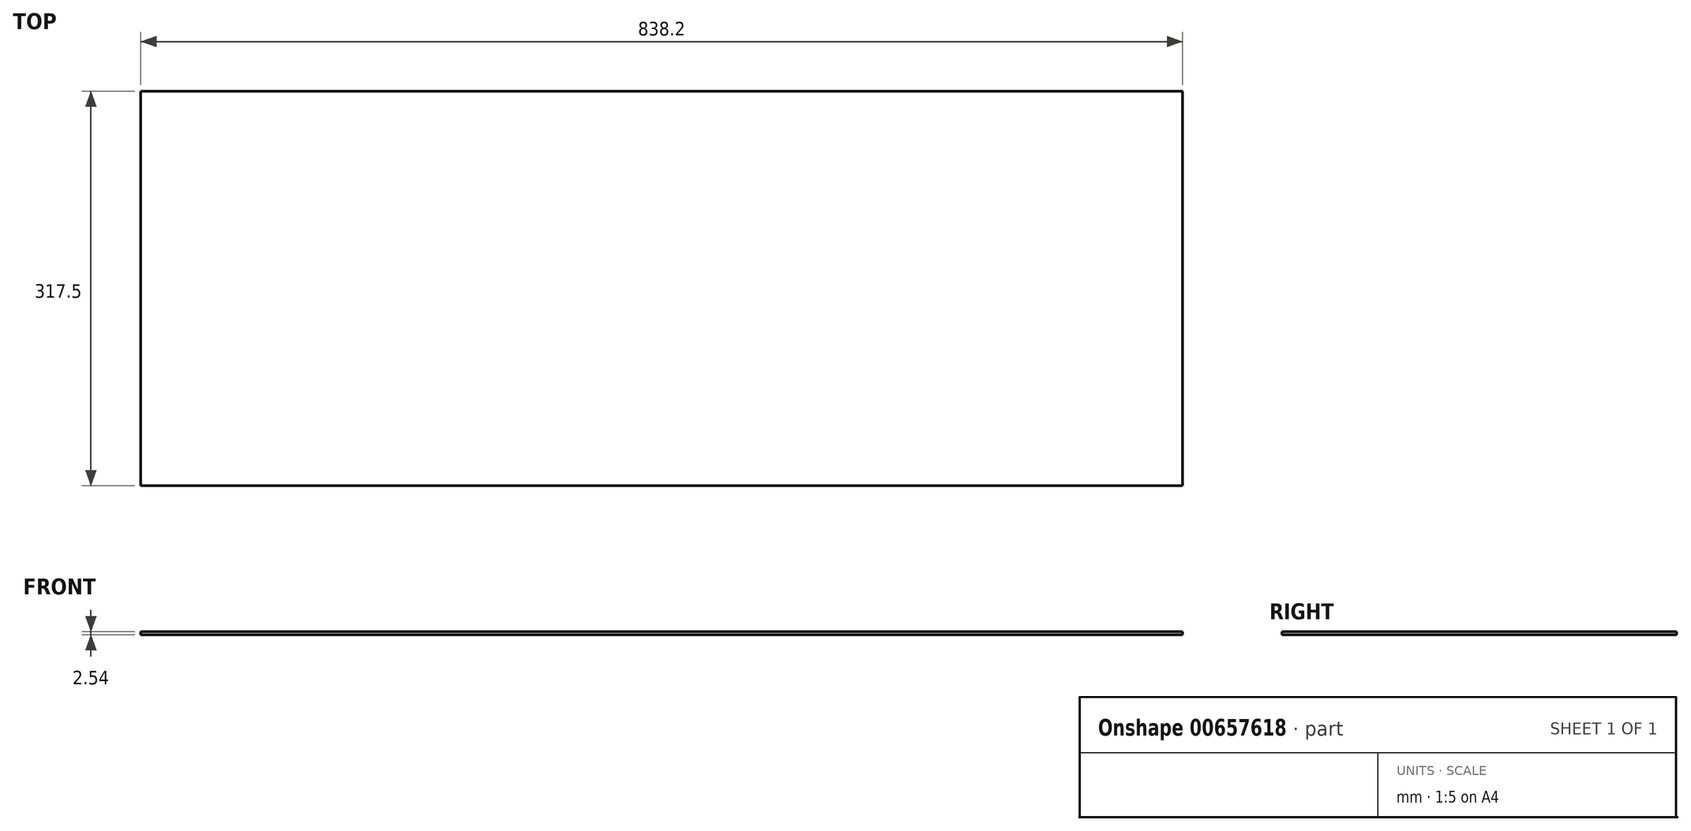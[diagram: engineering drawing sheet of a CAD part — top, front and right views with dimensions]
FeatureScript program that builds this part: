
annotation { "Feature Type Name" : "Feature", "Feature Type Description" : "" }
export const myFeature = defineFeature(function(context is Context, id is Id, definition is map)
    precondition{}
    {
        {
            var Q0;
            Q0=qCreatedBy(makeId("Top.planeOp"),FACE);
            var sketch = newSketch(context, id + "F0", { "sketchPlane" : qUnion([Q0])});
            skLineSegment(sketch, "E0.bottom", {"start": v(0, 0) * mm, "end": v(838.2, 0) * mm});
            skLineSegment(sketch, "E0.top", {"start": v(0, -317.5) * mm, "end": v(838.2, -317.5) * mm});
            skLineSegment(sketch, "E0.left", {"start": v(0, 0) * mm, "end": v(0, -317.5) * mm});
            skLineSegment(sketch, "E0.right", {"start": v(838.2, 0) * mm, "end": v(838.2, -317.5) * mm});
            skSolve(sketch);
        }
        {
            var Q0;
            Q0=makeQuery(id+"F0.imprint","IMPRINT",FACE,{"disambiguationData":[TD([[makeQuery(id+"F0.imprint","IMPRINT",EDGE,{"derivedFrom":sQuery(id+"F0.wireOp",EDGE,"E0.bottom")}),-1.0]])]});
            extrude(context, id + "F1", {"entities" : qUnion([Q0]), "depth" : 2.54 * mm, "offsetDistance" : 25.4 * mm});
        }
    });
